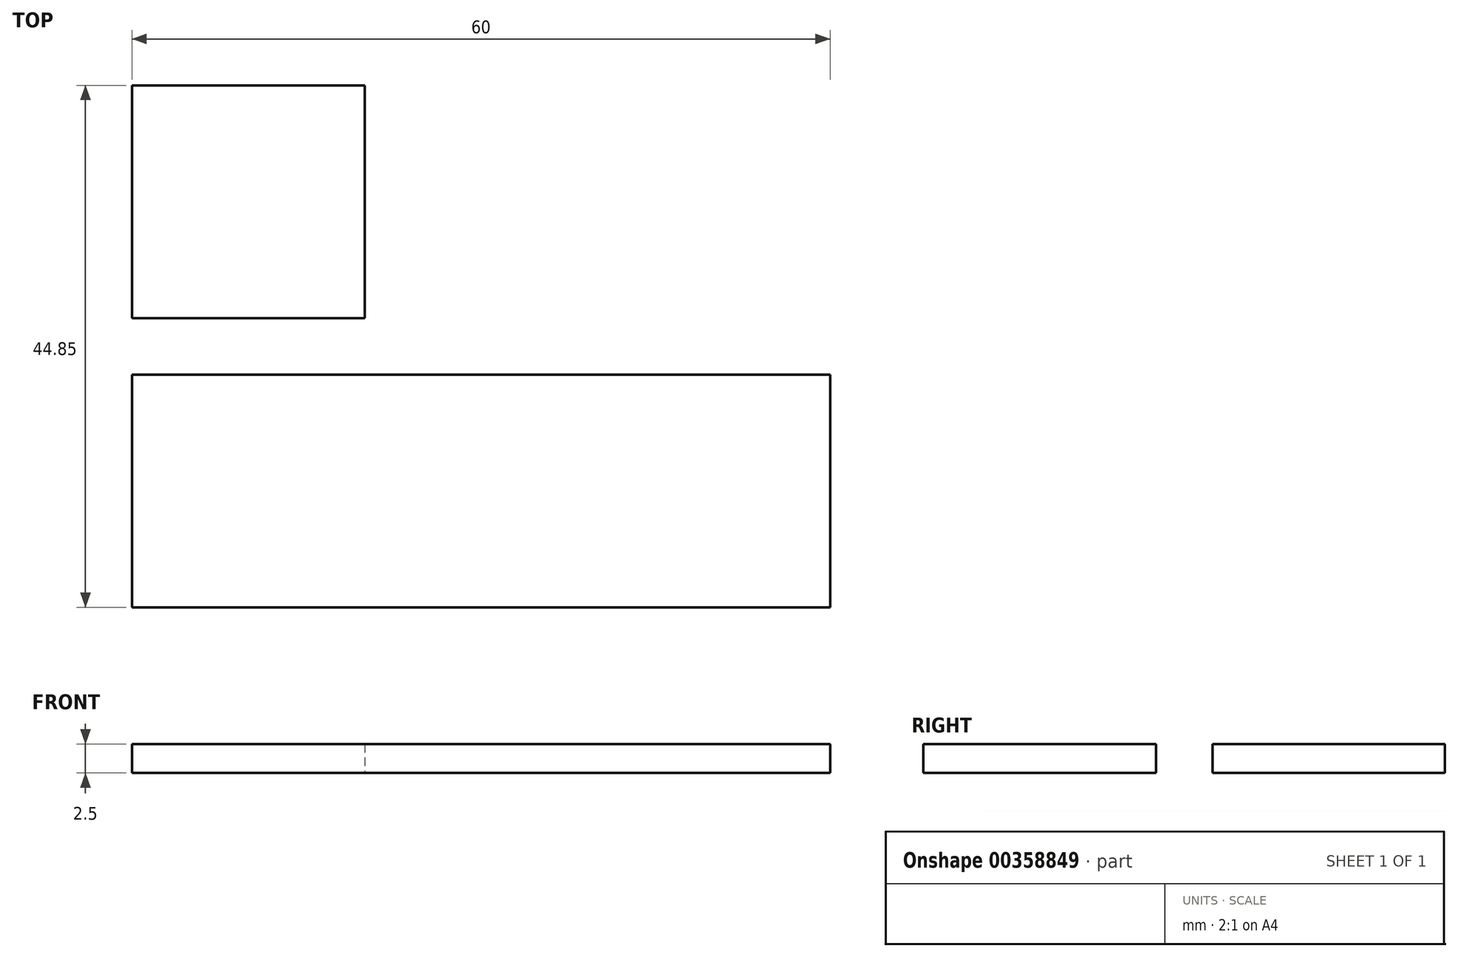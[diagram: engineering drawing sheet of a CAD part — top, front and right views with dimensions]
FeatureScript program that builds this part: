
annotation { "Feature Type Name" : "Feature", "Feature Type Description" : "" }
export const myFeature = defineFeature(function(context is Context, id is Id, definition is map)
    precondition{}
    {
        {
            var Q0;
            Q0=qCreatedBy(makeId("Top.planeOp"),FACE);
            var sketch = newSketch(context, id + "F0", { "sketchPlane" : qUnion([Q0])});
            skLineSegment(sketch, "E0.bottom", {"start": v(0, 0) * mm, "end": v(60, 0) * mm});
            skLineSegment(sketch, "E0.top", {"start": v(0, -20) * mm, "end": v(60, -20) * mm});
            skLineSegment(sketch, "E0.left", {"start": v(0, 0) * mm, "end": v(0, -20) * mm});
            skLineSegment(sketch, "E0.right", {"start": v(60, 0) * mm, "end": v(60, -20) * mm});
            skLineSegment(sketch, "E1.bottom", {"start": v(0, 4.85) * mm, "end": v(20, 4.85) * mm});
            skLineSegment(sketch, "E1.top", {"start": v(0, 24.85) * mm, "end": v(20, 24.85) * mm});
            skLineSegment(sketch, "E1.left", {"start": v(0, 4.85) * mm, "end": v(0, 24.85) * mm});
            skLineSegment(sketch, "E1.right", {"start": v(20, 4.85) * mm, "end": v(20, 24.85) * mm});
            skSolve(sketch);
        }
        {
            var Q0;
            Q0 = qSketchRegion(id + "F0", true);
            extrude(context, id + "F1", {"entities" : qUnion([Q0]), "depth" : 2.5 * mm});
        }
    });
